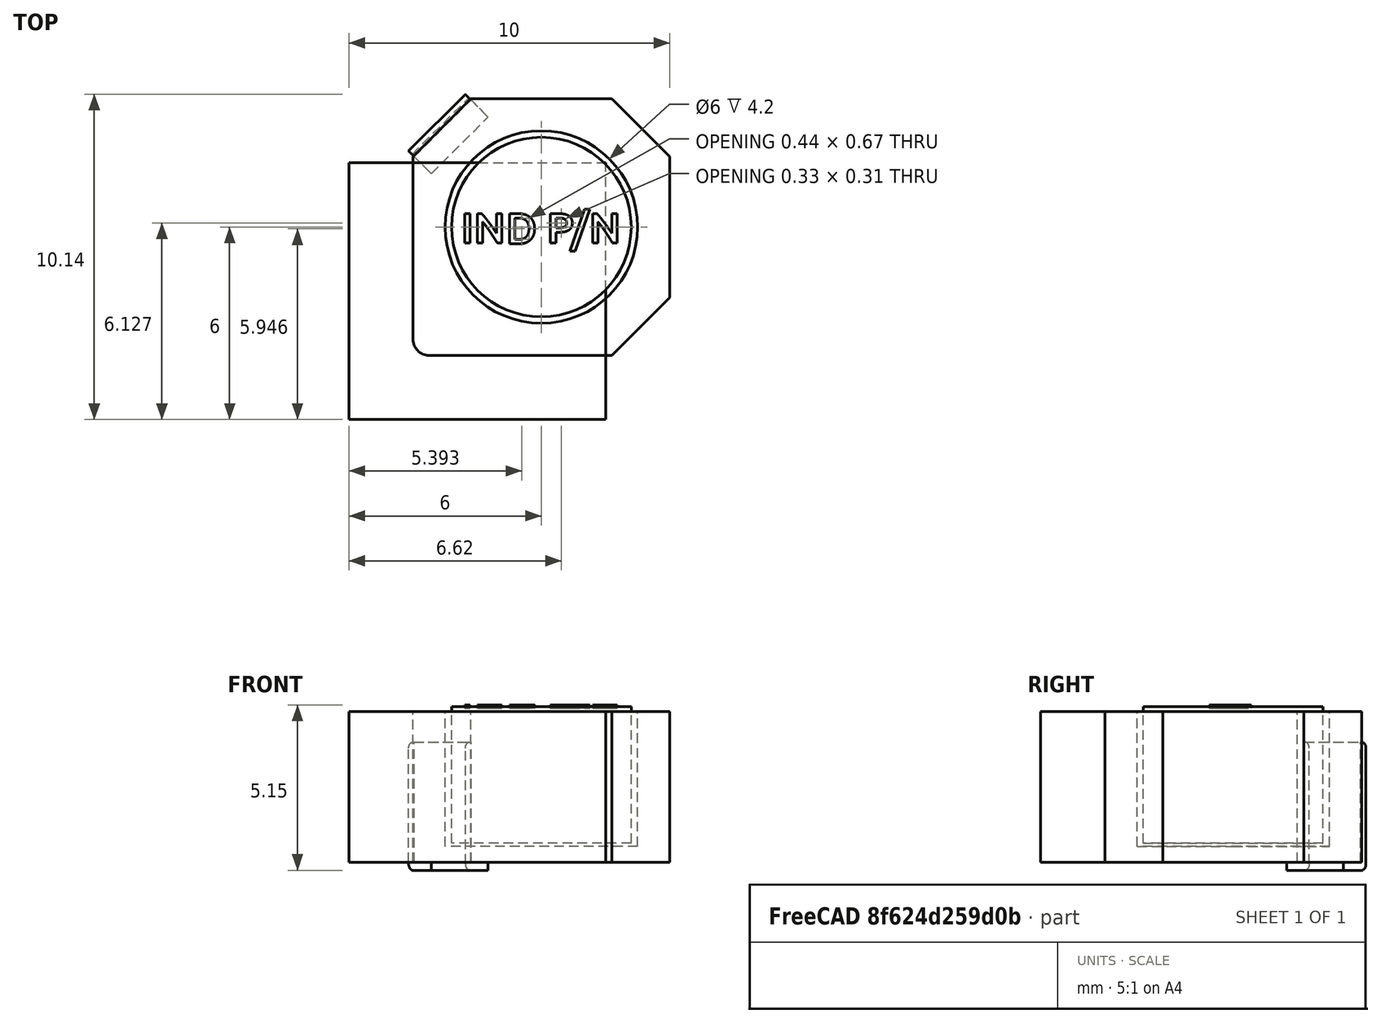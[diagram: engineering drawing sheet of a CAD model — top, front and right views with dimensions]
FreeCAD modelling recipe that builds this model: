
FCSTD DOCUMENT  (FreeCAD 0.18.1R)
Label: inductor_01
Comment: <userpath>/projects-git/kicon2019/data/Inductor_AGM0000CE20.pdf
License: All rights reserved
LicenseURL: http://en.wikipedia.org/wiki/All_rights_reserved
objects: Part::Box×3, Part::Fillet×2, Part::Cylinder×2, PartDesign::FeatureBase×1, PartDesign::Body×1, Part::Chamfer×1, Part::Cut×1, Part::MultiFuse×1, Part::Mirroring×1, Part::Part2DObjectPython×1, Part::Extrusion×1
note: 15 computed .brp shape members not serialized (recipe doc carries the construction recipe); baked Part::Feature solids carry a one-line shape summary decoded from their .brp

FEATURE [Part::Box] Box  label="Cube"
  AttacherType = Attacher::AttachEngine3D
  Height = 4.7
  Length = 8
  Placement = pos=(-4,-4,0) rot=(0,0,1;0rad)
  Width = 8
  expr: Placement.Base.y = -Cube.Length / 2
  expr: Placement.Base.x = -Cube.Length / 2
FEATURE [PartDesign::FeatureBase] BaseFeature
  BaseFeature = -> Box
FEATURE [PartDesign::Body] Body
  BaseFeature = -> Box
  Group = -> [BaseFeature]
  Origin = -> Origin
  Placement = pos=(-6,-6,0) rot=(0,0,1;0rad)
  Tip = -> BaseFeature
FEATURE [Part::Chamfer] Chamfer
  Base = -> Box
  Edges = 3 edges r=1.8: [Edge3,Edge5,Edge7]
FEATURE [Part::Fillet] Fillet
  Base = -> Chamfer
  Edges = 1 edges r=0.5: [Edge3]
FEATURE [Part::Cylinder] Cylinder
  Angle = 360
  AttacherType = Attacher::AttachEngine3D
  Height = 4.25
  Placement = pos=(0,0,0.5) rot=(0,0,1;0rad)
  Radius = 3
FEATURE [Part::Cut] Cut
  Base = -> Fillet
  Refine = true
  Tool = -> Cylinder
FEATURE [Part::Cylinder] Cylinder001
  Angle = 360
  AttacherType = Attacher::AttachEngine3D
  Height = 4.25
  Placement = pos=(0,0,0.6) rot=(0,0,1;0rad)
  Radius = 2.8
FEATURE [Part::Box] Box001  label="Cube001"
  AttacherType = Attacher::AttachEngine3D
  Height = 4
  Length = 2.5
  Placement = pos=(-1.25,-4.6,-0.25) rot=(0,0,1;0rad)
  Width = 0.25
FEATURE [Part::Box] Box002  label="Cube002"
  AttacherType = Attacher::AttachEngine3D
  Height = 0.25
  Length = 2.5
  Placement = pos=(-1.25,-4.45,-0.25) rot=(0,0,1;0rad)
  Width = 0.85
FEATURE [Part::Fillet] Fillet001
  Base = -> Box001
  Edges = 2 edges r=0.2: [Edge9,Edge10]
FEATURE [Part::MultiFuse] Fusion
  Placement = pos=(0,0,0) rot=(0,0,1;0.785398rad)
  Refine = true
  Shapes = -> [Fillet001,Box002]
FEATURE [Part::Mirroring] Part__Mirroring  label="Fusion (Mirror #1)"
  Base = (-1.68587e-07,1.19209e-07,1.75)
  Normal = (0,1,-1.19209e-07)
  Placement = pos=(0,0,0) rot=(0,0,1;1.5708rad)
  Source = -> Fusion
FEATURE [Part::Part2DObjectPython] ShapeString  # Draft 2D object (typed FeaturePython)
  FontFile = <path>
  Placement = pos=(-2.5,-0.5,4.8) rot=(0,0,1;0rad)
  Size = 0.5
  String = IND P/N
  Support = -> [Cylinder001]
  Tracking = 0
FEATURE [Part::Extrusion] Extrude
  Base = -> ShapeString
  Dir = (0,0,1)
  DirMode = 2
  FaceMakerClass = Part::FaceMakerBullseye
  LengthFwd = 0.1
  LengthRev = 0
  Solid = true
  Symmetric = false
note: 1 file-system path scrubbed to <path> (originals preserved in the JSON sidecar)
